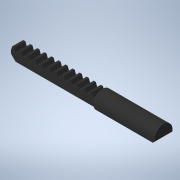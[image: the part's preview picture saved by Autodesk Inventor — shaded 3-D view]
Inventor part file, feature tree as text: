
AUTODESK INVENTOR PART (.ipt)
format: ipt  version: 2021 (Build 250183000, 183)  size: 199,680 bytes
history: native  units: mm
features: sketch x4, extrude x3, chamfer x2, projected_geometry x2, revolve x1, pattern_linear x1
ambient origin geometry x8: Origin, YZ Plane, XZ Plane, XY Plane, X Axis, Y Axis, Z Axis, Center Point
bodies: Body1 (feature_tree)
feature tree (13):
  revolve  "Revolution1"  [1 undecoded]
  extrude  "Extrusion5"  Depth=53.0mm TaperAngle=0.0deg
  extrude  "Extrusion10"  Depth=47.0mm
  extrude  "Extrusion11"  Depth=6.0mm TaperAngle=0.0deg
  pattern_linear  "Rectangular Pattern1"  Spacing1=1.2mm  [1 undecoded]
  chamfer  "Chamfer5"  Distance=2.0mm
  chamfer  "Chamfer6"  Distance=12.217305mm
  sketch  "Sketch5"  dims[d91=90.0deg d95=4.9mm]
  sketch  "Sketch6"  dims[d96=3.0mm d97=53.0mm d98=0.0mm]
  projected_geometry  "Projected Loop5"
  sketch  "Sketch11"  dims[d106=33.5mm d137=47.0mm]
  projected_geometry  "Projected Loop7"
  sketch  "Sketch12"  dims[d138=6.4mm d144=6.0mm d145=0.0mm d152=1.2mm d153=2.0mm d154=12.217305mm d155=1.2mm d156=0.0mm d157=0.0mm d158=120.0mm d160=3.855mm d161=2.0mm d162=2.0mm d163=45.0deg d164=2.5mm d165=2.0mm d166=45.0deg]
note: 2 required parameter values undecoded (feature->parameter linkage not recoverable at this tier; creation-order binding heuristic only, values carry confidence <= 0.55)